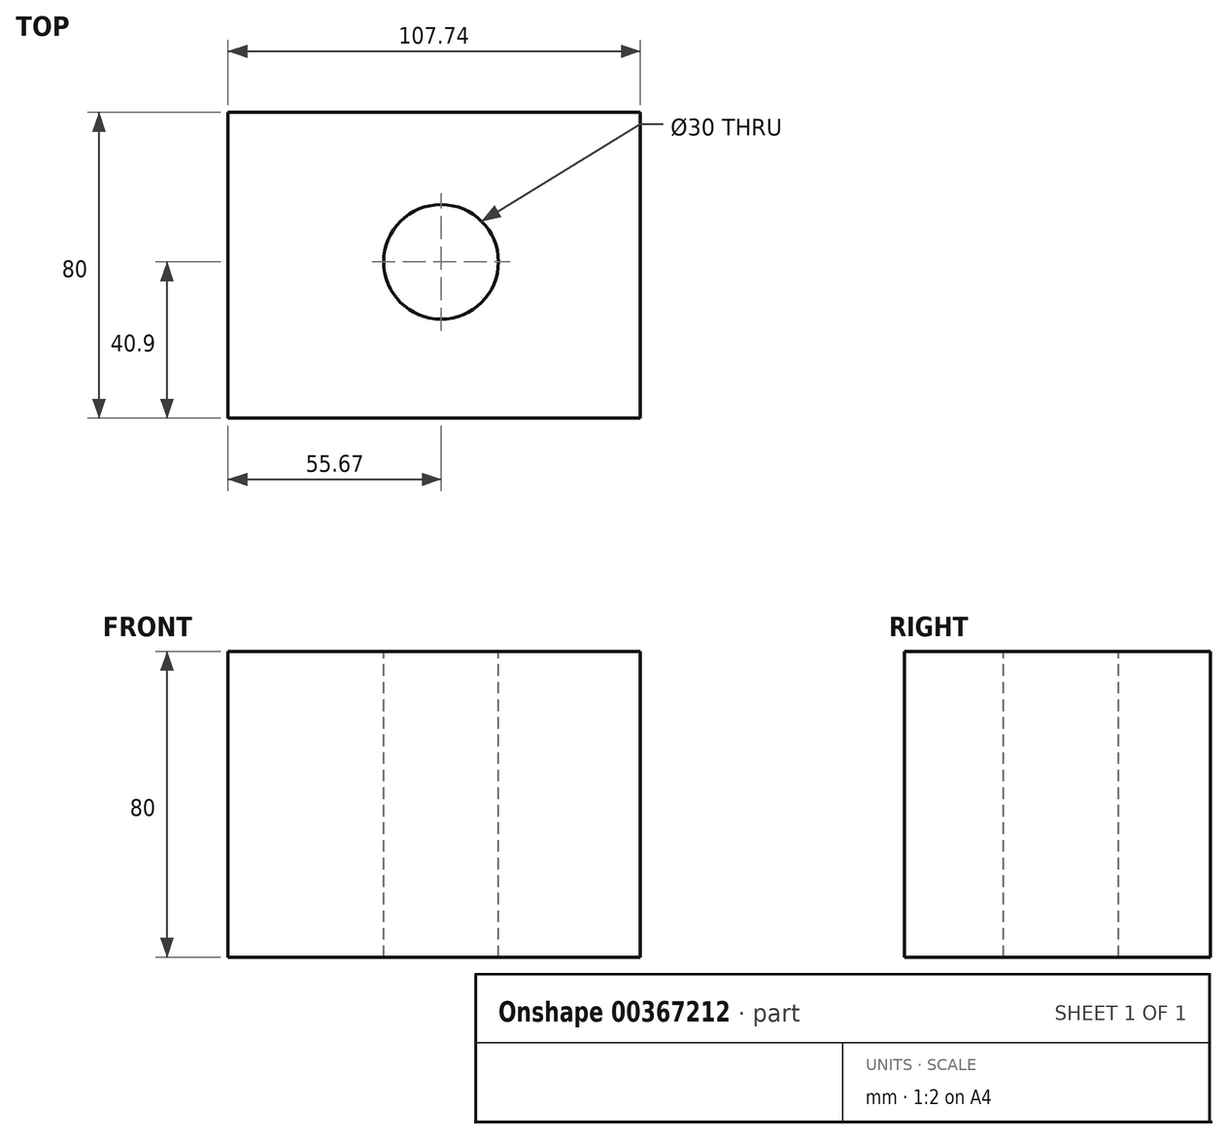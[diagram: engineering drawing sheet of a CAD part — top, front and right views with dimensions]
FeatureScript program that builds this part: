
annotation { "Feature Type Name" : "Feature", "Feature Type Description" : "" }
export const myFeature = defineFeature(function(context is Context, id is Id, definition is map)
    precondition{}
    {
        {
            var Q0;
            Q0=qCreatedBy(makeId("Top.planeOp"),FACE);
            var sketch = newSketch(context, id + "F0", { "sketchPlane" : qUnion([Q0])});
            skLineSegment(sketch, "E0.bottom", {"start": v(-55.67, 39.1) * mm, "end": v(52.07, 39.1) * mm});
            skLineSegment(sketch, "E0.top", {"start": v(-55.67, -40.9) * mm, "end": v(52.07, -40.9) * mm});
            skLineSegment(sketch, "E0.left", {"start": v(-55.67, 39.1) * mm, "end": v(-55.67, -40.9) * mm});
            skLineSegment(sketch, "E0.right", {"start": v(52.07, 39.1) * mm, "end": v(52.07, -40.9) * mm});
            skSolve(sketch);
        }
        {
            var Q0;
            Q0=makeQuery(id+"F0.imprint","IMPRINT",FACE,{"disambiguationData":[TD([[makeQuery(id+"F0.imprint","IMPRINT",EDGE,{"derivedFrom":sQuery(id+"F0.wireOp",EDGE,"E0.bottom")}),-1.0]])]});
            var Q1;
            Q1 = qSketchRegion(id + "FEqAUkbeDbnYBgL_1", true);
            extrude(context, id + "F1", {"entities" : qUnion([Q0, Q1]), "depth" : 80 * mm});
        }
        {
            var Q0;
            Q0=makeQuery(id+"F1.opExtrude","CAP_FACE",FACE,{"disambiguationData":[OSD([sQuery(id+"F0.wireOp",EDGE,"E0.bottom"),sQuery(id+"F0.wireOp",EDGE,"E0.top"),sQuery(id+"F0.wireOp",EDGE,"E0.left"),sQuery(id+"F0.wireOp",EDGE,"E0.right")])],"isStart":false});
            var sketch = newSketch(context, id + "F2", { "sketchPlane" : qUnion([Q0])});
            skCircle(sketch, "E1", {"center": v(0, 0) * mm, "radius": 15 * mm});
            skSolve(sketch);
        }
        {
            var Q0;
            Q0=makeQuery(id+"F2.imprint","IMPRINT",FACE,{"disambiguationData":[TD([[makeQuery(id+"F2.imprint","IMPRINT",EDGE,{"derivedFrom":sQuery(id+"F2.wireOp",EDGE,"E1")}),1.0]])]});
            extrude(context, id + "F3", {"entities" : qUnion([Q0]), "operationType" : NewBodyOperationType.REMOVE, "endBound" : BoundingType.THROUGH_ALL, "oppositeDirection" : true, "depth" : 25 * mm});
        }
    });
